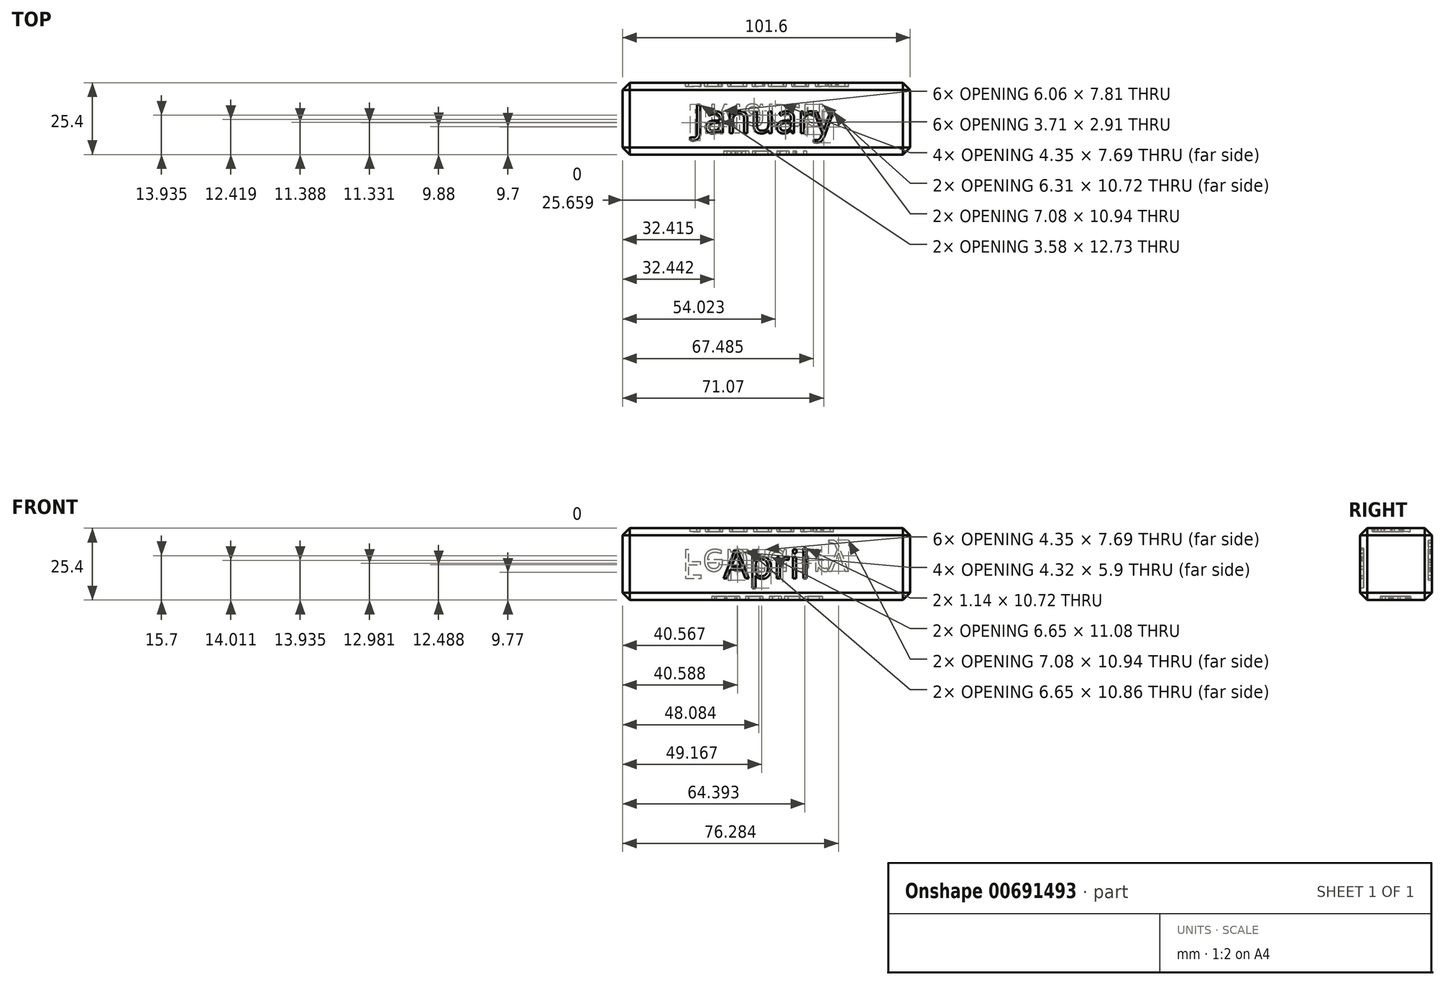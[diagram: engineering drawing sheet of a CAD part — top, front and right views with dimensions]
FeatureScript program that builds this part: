
annotation { "Feature Type Name" : "Feature", "Feature Type Description" : "" }
export const myFeature = defineFeature(function(context is Context, id is Id, definition is map)
    precondition{}
    {
        {
            var Q0;
            Q0=qCreatedBy(makeId("Top.planeOp"),FACE);
            var sketch = newSketch(context, id + "F0", { "sketchPlane" : qUnion([Q0])});
            skLineSegment(sketch, "E0.bottom", {"start": v(50.8, 12.7) * mm, "end": v(-50.8, 12.7) * mm});
            skLineSegment(sketch, "E0.top", {"start": v(50.8, -12.7) * mm, "end": v(-50.8, -12.7) * mm});
            skLineSegment(sketch, "E0.left", {"start": v(50.8, 12.7) * mm, "end": v(50.8, -12.7) * mm});
            skLineSegment(sketch, "E0.right", {"start": v(-50.8, 12.7) * mm, "end": v(-50.8, -12.7) * mm});
            skPoint(sketch, "E0.middle", {"position": v(0, 0) * mm});
            skSolve(sketch);
        }
        {
            var Q0;
            Q0 = qSketchRegion(id + "F0", true);
            extrude(context, id + "F1", {"entities" : qUnion([Q0]), "depth" : 12.7 * mm, "offsetDistance" : 25.4 * mm, "hasSecondDirection" : true, "secondDirectionOppositeDirection" : true, "secondDirectionDepth" : 12.7 * mm});
        }
        {
            var Q0;
            Q0=makeQuery(id+"F1.opExtrude","CAP_FACE",FACE,{"disambiguationData":[OSD([sQuery(id+"F0.wireOp",EDGE,"E0.bottom"),sQuery(id+"F0.wireOp",EDGE,"E0.top"),sQuery(id+"F0.wireOp",EDGE,"E0.left"),sQuery(id+"F0.wireOp",EDGE,"E0.right")])],"isStart":false});
            var Q1;
            Q1=makeQuery(id+"F1.opExtrude","SWEPT_FACE",FACE,{"disambiguationData":[OSD([sQuery(id+"F0.wireOp",EDGE,"E0.bottom")])]});
            var Q2;
            Q2=makeQuery(id+"F1.opExtrude","SWEPT_FACE",FACE,{"disambiguationData":[OSD([sQuery(id+"F0.wireOp",EDGE,"E0.right")])]});
            var Q3;
            Q3=makeQuery(id+"F1.opExtrude","CAP_FACE",FACE,{"disambiguationData":[OSD([sQuery(id+"F0.wireOp",EDGE,"E0.bottom"),sQuery(id+"F0.wireOp",EDGE,"E0.top"),sQuery(id+"F0.wireOp",EDGE,"E0.left"),sQuery(id+"F0.wireOp",EDGE,"E0.right")])],"isStart":true});
            var Q4;
            Q4=makeQuery(id+"F1.opExtrude","SWEPT_FACE",FACE,{"disambiguationData":[OSD([sQuery(id+"F0.wireOp",EDGE,"E0.left")])]});
            chamfer(context, id + "F2", {"entities" : qUnion([Q0, Q1, Q2, Q3, Q4]), "width" : 2.54 * mm, "tangentPropagation" : true});
        }
        {
            var Q0;
            Q0=makeQuery(id+"F1.opExtrude","CAP_FACE",FACE,{"disambiguationData":[OSD([sQuery(id+"F0.wireOp",EDGE,"E0.bottom"),sQuery(id+"F0.wireOp",EDGE,"E0.top"),sQuery(id+"F0.wireOp",EDGE,"E0.left"),sQuery(id+"F0.wireOp",EDGE,"E0.right")])],"isStart":false});
            var sketch = newSketch(context, id + "F3", { "sketchPlane" : qUnion([Q0])});
            skText(sketch, "E1", { "text": "January", "fontName": "OpenSans-Regular.ttf"});
            skLineSegment(sketch, "E2", {"start": v(-25.83, 0) * mm, "end": v(-58.59, 0) * mm, "construction": true});
            const initialGuessF3  = {"E1": [-0.02583, -0.00508, 1, 0, 0.01016]};
            skSetInitialGuess(sketch, initialGuessF3);
            skSolve(sketch);
        }
        {
            var Q0;
            Q0 = qSketchRegion(id + "F3", true);
            extrude(context, id + "F4", {"entities" : qUnion([Q0]), "operationType" : NewBodyOperationType.REMOVE, "oppositeDirection" : true, "depth" : 1.27 * mm, "offsetDistance" : 25.4 * mm});
        }
        {
            var Q0;
            Q0=makeQuery(id+"F1.opExtrude","SWEPT_FACE",FACE,{"disambiguationData":[OSD([sQuery(id+"F0.wireOp",EDGE,"E0.bottom")])]});
            var sketch = newSketch(context, id + "F5", { "sketchPlane" : qUnion([Q0])});
            skText(sketch, "E3", { "text": "February", "fontName": "OpenSans-Regular.ttf"});
            skLineSegment(sketch, "E4", {"start": v(66, 0) * mm, "end": v(29.95, 0) * mm, "construction": true});
            const initialGuessF5  = {"E3": [0.02995, 0.00508, -1, 0, 0.01016]};
            skSetInitialGuess(sketch, initialGuessF5);
            skSolve(sketch);
        }
        {
            var Q0;
            Q0 = qSketchRegion(id + "F5", true);
            extrude(context, id + "F6", {"entities" : qUnion([Q0]), "operationType" : NewBodyOperationType.REMOVE, "oppositeDirection" : true, "depth" : 1.27 * mm, "offsetDistance" : 25.4 * mm});
        }
        {
            var Q0;
            Q0=makeQuery(id+"F1.opExtrude","CAP_FACE",FACE,{"disambiguationData":[OSD([sQuery(id+"F0.wireOp",EDGE,"E0.bottom"),sQuery(id+"F0.wireOp",EDGE,"E0.top"),sQuery(id+"F0.wireOp",EDGE,"E0.left"),sQuery(id+"F0.wireOp",EDGE,"E0.right")])],"isStart":true});
            var sketch = newSketch(context, id + "F7", { "sketchPlane" : qUnion([Q0])});
            skText(sketch, "E5", { "text": "March", "fontName": "OpenSans-Regular.ttf"});
            skLineSegment(sketch, "E6", {"start": v(-20.75, 0) * mm, "end": v(-54.83, 0) * mm, "construction": true});
            const initialGuessF7  = {"E5": [-0.02075, -0.00508, 1, 0, 0.01016]};
            skSetInitialGuess(sketch, initialGuessF7);
            skSolve(sketch);
        }
        {
            var Q0;
            Q0 = qSketchRegion(id + "F7", true);
            extrude(context, id + "F8", {"entities" : qUnion([Q0]), "operationType" : NewBodyOperationType.REMOVE, "oppositeDirection" : true, "depth" : 1.27 * mm, "offsetDistance" : 25.4 * mm});
        }
        {
            var Q0;
            Q0=makeQuery(id+"F1.opExtrude","SWEPT_FACE",FACE,{"disambiguationData":[OSD([sQuery(id+"F0.wireOp",EDGE,"E0.top")])]});
            var sketch = newSketch(context, id + "F9", { "sketchPlane" : qUnion([Q0])});
            skText(sketch, "E7", { "text": "April", "fontName": "OpenSans-Regular.ttf"});
            skLineSegment(sketch, "E8", {"start": v(-15.1, 0) * mm, "end": v(-59.47, 0) * mm, "construction": true});
            const initialGuessF9  = {"E7": [-0.0151, -0.00508, 1, 0, 0.01016]};
            skSetInitialGuess(sketch, initialGuessF9);
            skSolve(sketch);
        }
        {
            var Q0;
            Q0 = qSketchRegion(id + "F9", true);
            extrude(context, id + "F10", {"entities" : qUnion([Q0]), "operationType" : NewBodyOperationType.REMOVE, "oppositeDirection" : true, "depth" : 1.27 * mm, "offsetDistance" : 25.4 * mm});
        }
    });
